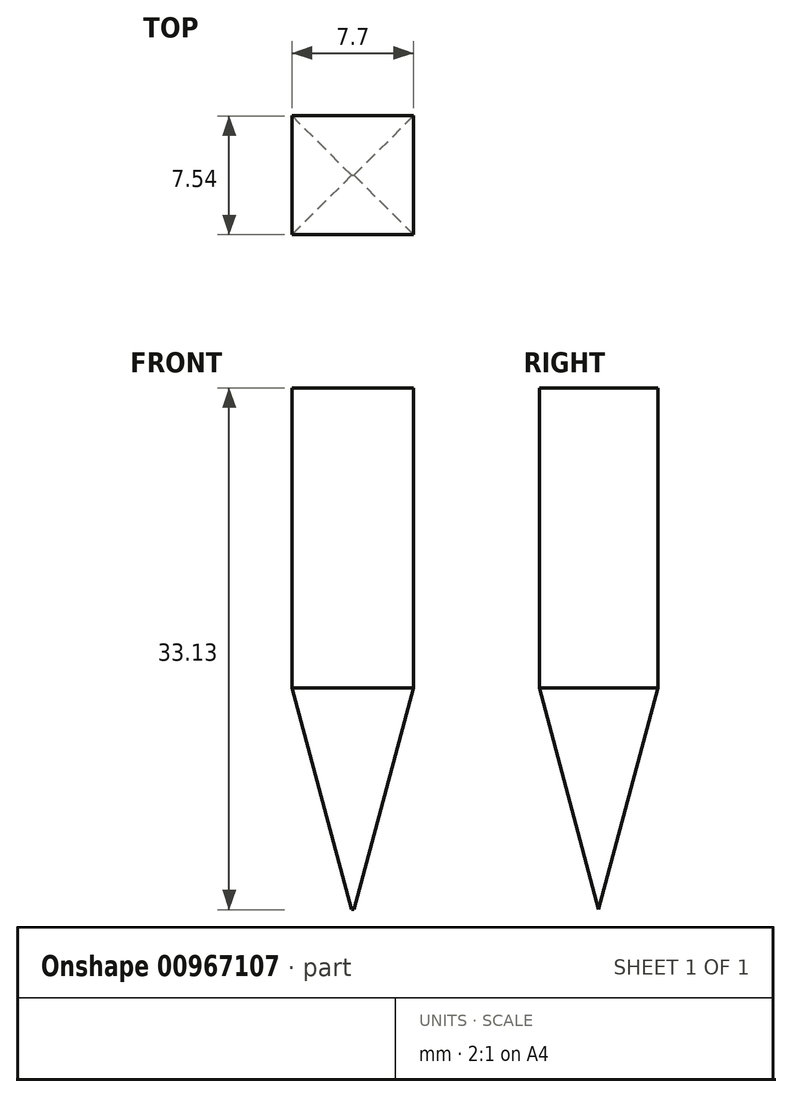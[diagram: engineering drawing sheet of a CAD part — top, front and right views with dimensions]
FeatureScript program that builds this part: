
annotation { "Feature Type Name" : "Feature", "Feature Type Description" : "" }
export const myFeature = defineFeature(function(context is Context, id is Id, definition is map)
    precondition{}
    {
        {
            var Q0;
            Q0=qCreatedBy(makeId("Top.planeOp"),FACE);
            var sketch = newSketch(context, id + "F0", { "sketchPlane" : qUnion([Q0])});
            skPoint(sketch, "E0.middle", {"position": v(0, 0) * mm});
            skLineSegment(sketch, "E1.bottom", {"start": v(3.85, 3.77) * mm, "end": v(-3.85, 3.77) * mm});
            skLineSegment(sketch, "E1.top", {"start": v(3.85, -3.77) * mm, "end": v(-3.85, -3.77) * mm});
            skLineSegment(sketch, "E1.left", {"start": v(3.85, 3.77) * mm, "end": v(3.85, -3.77) * mm});
            skLineSegment(sketch, "E1.right", {"start": v(-3.85, 3.77) * mm, "end": v(-3.85, -3.77) * mm});
            skSolve(sketch);
        }
        {
            var Q0;
            Q0=makeQuery(id+"F0.imprint","IMPRINT",FACE,{"disambiguationData":[TD([[makeQuery(id+"F0.imprint","IMPRINT",EDGE,{"derivedFrom":sQuery(id+"F0.wireOp",EDGE,"E1.bottom")}),1.0]])]});
            extrude(context, id + "F1", {"entities" : qUnion([Q0]), "depth" : 19.05 * mm, "offsetDistance" : 25.4 * mm});
        }
        {
            var Q0;
            Q0=makeQuery(id+"F0.imprint","IMPRINT",FACE,{"disambiguationData":[TD([[makeQuery(id+"F0.imprint","IMPRINT",EDGE,{"derivedFrom":sQuery(id+"F0.wireOp",EDGE,"E1.bottom")}),1.0]])]});
            extrude(context, id + "F2", {"entities" : qUnion([Q0]), "operationType" : NewBodyOperationType.ADD, "oppositeDirection" : true, "depth" : 25.4 * mm, "offsetDistance" : 25.4 * mm, "hasDraft" : true, "draftAngle" : 15 * degree, "draftPullDirection" : true});
        }
    });
